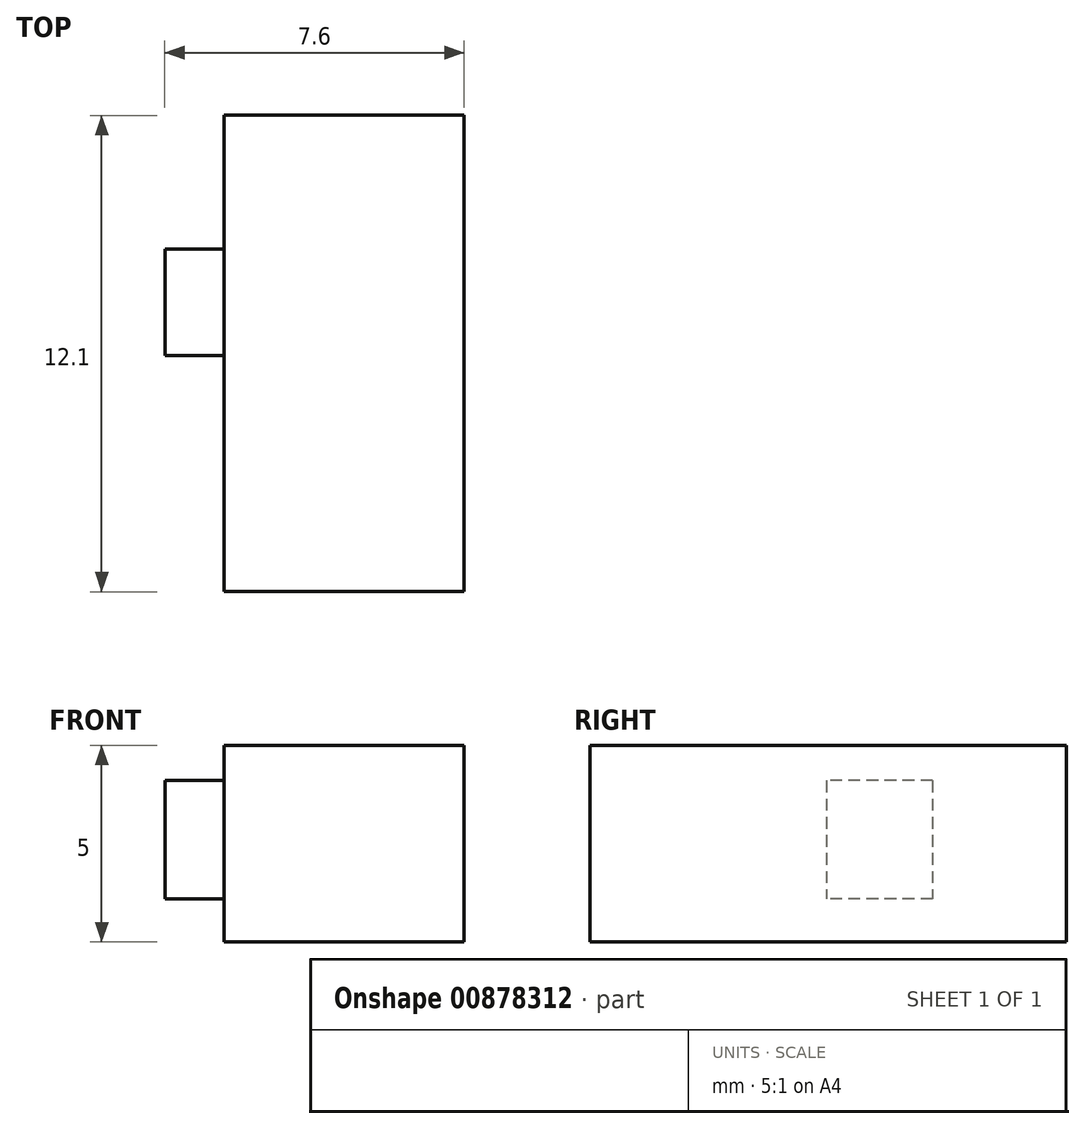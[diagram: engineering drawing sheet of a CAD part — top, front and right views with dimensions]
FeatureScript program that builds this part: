
annotation { "Feature Type Name" : "Feature", "Feature Type Description" : "" }
export const myFeature = defineFeature(function(context is Context, id is Id, definition is map)
    precondition{}
    {
        {
            var Q0;
            Q0=qCreatedBy(makeId("Top.planeOp"),FACE);
            var sketch = newSketch(context, id + "F0", { "sketchPlane" : qUnion([Q0])});
            skLineSegment(sketch, "E0.bottom", {"start": v(-24.13, 5.73) * mm, "end": v(-18.03, 5.73) * mm});
            skLineSegment(sketch, "E0.top", {"start": v(-24.13, -6.37) * mm, "end": v(-18.03, -6.37) * mm});
            skLineSegment(sketch, "E0.left", {"start": v(-24.13, 5.73) * mm, "end": v(-24.13, -6.37) * mm});
            skLineSegment(sketch, "E0.right", {"start": v(-18.03, 5.73) * mm, "end": v(-18.03, -6.37) * mm});
            skSolve(sketch);
        }
        {
            var Q0;
            Q0 = qSketchRegion(id + "F0", true);
            extrude(context, id + "F1", {"entities" : qUnion([Q0]), "depth" : 5 * mm, "offsetDistance" : 25 * mm});
        }
        {
            var Q0;
            Q0=makeQuery(id+"F1.opExtrude","SWEPT_FACE",FACE,{"disambiguationData":[OSD([sQuery(id+"F0.wireOp",EDGE,"E0.left")])]});
            var sketch = newSketch(context, id + "F2", { "sketchPlane" : qUnion([Q0])});
            skLineSegment(sketch, "E1.bottom", {"start": v(-2.33, 4.1) * mm, "end": v(0.37, 4.1) * mm});
            skLineSegment(sketch, "E1.top", {"start": v(-2.33, 1.1) * mm, "end": v(0.37, 1.1) * mm});
            skLineSegment(sketch, "E1.left", {"start": v(-2.33, 4.1) * mm, "end": v(-2.33, 1.1) * mm});
            skLineSegment(sketch, "E1.right", {"start": v(0.37, 4.1) * mm, "end": v(0.37, 1.1) * mm});
            skSolve(sketch);
        }
        {
            var Q0;
            Q0=makeQuery(id+"F2.imprint","IMPRINT",FACE,{"disambiguationData":[TD([[makeQuery(id+"F2.imprint","IMPRINT",EDGE,{"derivedFrom":sQuery(id+"F2.wireOp",EDGE,"E1.bottom")}),-1.0]])]});
            extrude(context, id + "F3", {"entities" : qUnion([Q0]), "operationType" : NewBodyOperationType.ADD, "depth" : 1.5 * mm, "offsetDistance" : 25 * mm});
        }
    });
